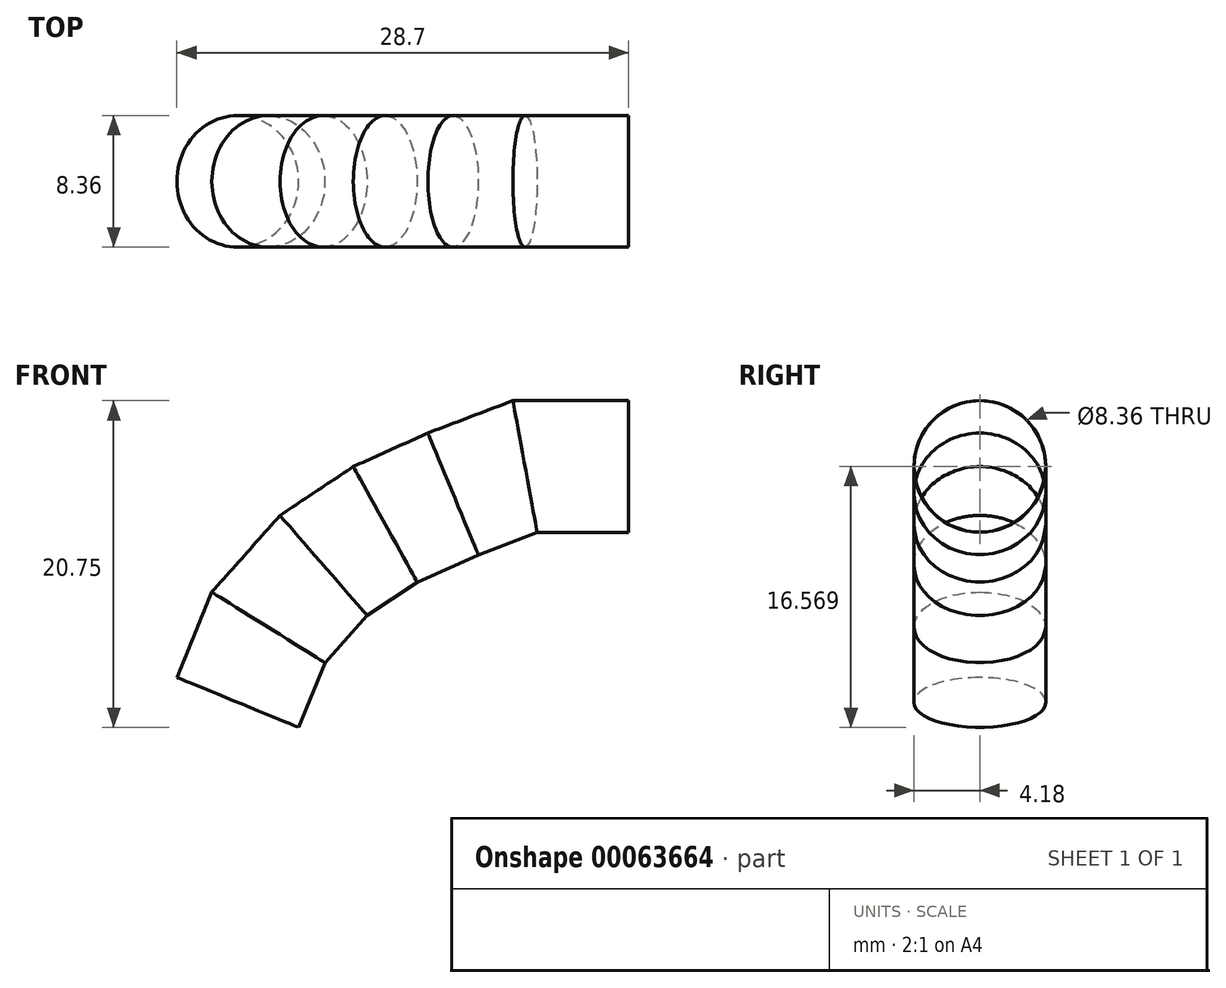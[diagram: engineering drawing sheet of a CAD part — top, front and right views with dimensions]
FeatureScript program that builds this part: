
annotation { "Feature Type Name" : "Feature", "Feature Type Description" : "" }
export const myFeature = defineFeature(function(context is Context, id is Id, definition is map)
    precondition{}
    {
        {
            var Q0;
            Q0=qCreatedBy(makeId("Front.planeOp"),FACE);
            var sketch = newSketch(context, id + "F0", { "sketchPlane" : qUnion([Q0])});
            skLineSegment(sketch, "E0", {"start": v(-24.43, 0) * mm, "end": v(-22.5, 4.7) * mm});
            skLineSegment(sketch, "E1", {"start": v(-22.5, 4.7) * mm, "end": v(-19.1, 8.53) * mm});
            skLineSegment(sketch, "E2", {"start": v(-19.1, 8.53) * mm, "end": v(-15.26, 11.1) * mm});
            skLineSegment(sketch, "E3", {"start": v(-15.26, 11.1) * mm, "end": v(-10.99, 13.01) * mm});
            skLineSegment(sketch, "E4", {"start": v(-10.99, 13.01) * mm, "end": v(-6.5, 14.72) * mm});
            skLineSegment(sketch, "E5", {"start": v(-6.5, 14.72) * mm, "end": v(0, 14.72) * mm});
            skSolve(sketch);
        }
        {
            var Q0;
            Q0=qCreatedBy(makeId("Top.planeOp"),FACE);
            var sketch = newSketch(context, id + "F1", { "sketchPlane" : qUnion([Q0])});
            skCircle(sketch, "E6", {"center": v(-24.86, 0) * mm, "radius": 6.8 * mm});
            skSolve(sketch);
        }
        {
            var Q0;
            Q0=qCreatedBy(makeId("Right.planeOp"),FACE);
            var sketch = newSketch(context, id + "F2", { "sketchPlane" : qUnion([Q0])});
            skCircle(sketch, "E7", {"center": v(0, 15.15) * mm, "radius": 4.18 * mm});
            skSolve(sketch);
        }
        {
            var Q0;
            Q0 = qSketchRegion(id + "F1", true);
            var Q1;
            Q1 = qConstructionFilter(qBodyType(qCreatedBy(id + "F2" ,EDGE), BodyType.WIRE), ConstructionObject.NO);
            var Q2;
            Q2 = qConstructionFilter(qBodyType(qCreatedBy(id + "F0" ,EDGE), BodyType.WIRE), ConstructionObject.NO);
            sweep(context, id + "F3", {"bodyType" : ToolBodyType.SURFACE, "operationType" : NewBodyOperationType.REMOVE, "profiles" : qUnion([Q0]), "surfaceProfiles" : qUnion([Q1]), "path" : qUnion([Q2])});
        }
    });
